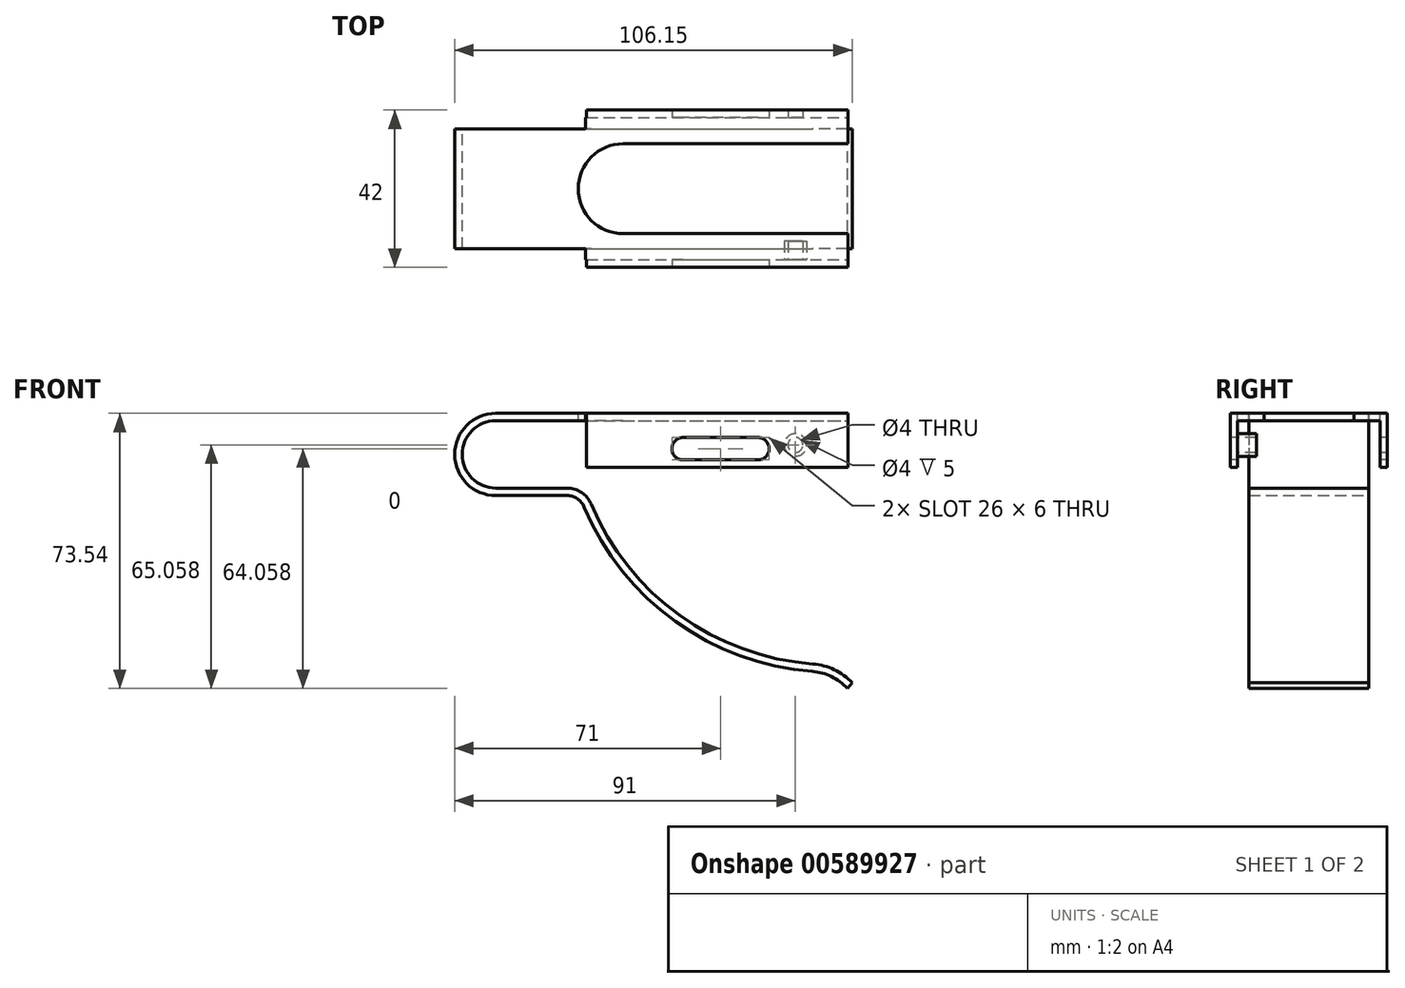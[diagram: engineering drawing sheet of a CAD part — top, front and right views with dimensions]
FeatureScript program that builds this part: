
annotation { "Feature Type Name" : "Feature", "Feature Type Description" : "" }
export const myFeature = defineFeature(function(context is Context, id is Id, definition is map)
    precondition{}
    {
        {
            var Q0;
            Q0=qCreatedBy(makeId("Front.planeOp"),FACE);
            var sketch = newSketch(context, id + "F0", { "sketchPlane" : qUnion([Q0])});
            skArc(sketch, "E0", {"start": v(0, 11) * mm, "mid": v(-11, 0) * mm, "end": v(0, -11) * mm});
            skLineSegment(sketch, "E1", {"start": v(0, 11) * mm, "end": v(94, 11) * mm});
            skLineSegment(sketch, "E2", {"start": v(0, -11) * mm, "end": v(19, -11) * mm});
            skArc(sketch, "E3", {"start": v(23.61, -14.06) * mm, "mid": v(47.9, -44.6) * mm, "end": v(84.55, -58) * mm});
            skArc(sketch, "E4", {"start": v(93.86, -62.54) * mm, "mid": v(89.64, -59.38) * mm, "end": v(84.55, -58) * mm});
            skPoint(sketch, "E5.visualSharp", {"position": v(22.4, -11) * mm});
            skArc(sketch, "E5.filletArc", {"start": v(23.61, -14.06) * mm, "mid": v(21.77, -11.84) * mm, "end": v(19, -11) * mm});
            skLineSegment(sketch, "E6.0", {"start": v(0, 9) * mm, "end": v(94, 9) * mm});
            skArc(sketch, "E6.1", {"start": v(0, 9) * mm, "mid": v(-9, 0) * mm, "end": v(0, -9) * mm});
            skArc(sketch, "E6.2", {"start": v(95.15, -61) * mm, "mid": v(90.4, -57.52) * mm, "end": v(84.7, -56) * mm});
            skArc(sketch, "E6.3", {"start": v(25.45, -13.3) * mm, "mid": v(49.07, -42.99) * mm, "end": v(84.7, -56) * mm});
            skArc(sketch, "E6.4", {"start": v(25.45, -13.3) * mm, "mid": v(22.88, -10.17) * mm, "end": v(19, -9) * mm});
            skLineSegment(sketch, "E6.5", {"start": v(0, -9) * mm, "end": v(19, -9) * mm});
            skLineSegment(sketch, "E7", {"start": v(94, 9) * mm, "end": v(94, 11) * mm});
            skLineSegment(sketch, "E8", {"start": v(93.86, -62.54) * mm, "end": v(95.15, -61) * mm});
            skLineSegment(sketch, "E9", {"start": v(97.48, -61.06) * mm, "end": v(102.9, -61.06) * mm, "construction": true});
            skPoint(sketch, "E10.newPointA", {"position": v(19, -11) * mm});
            skSolve(sketch);
        }
        {
            var Q0;
            Q0 = qSketchRegion(id + "F0", true);
            extrude(context, id + "F1", {"entities" : qUnion([Q0]), "depth" : 16 * mm, "offsetDistance" : 25 * mm});
        }
        {
            var Q0;
            Q0=makeQuery(id+"F1.opExtrude","SWEPT_FACE",FACE,{"disambiguationData":[OSD([sQuery(id+"F0.wireOp",EDGE,"E1")])]});
            var sketch = newSketch(context, id + "F2", { "sketchPlane" : qUnion([Q0])});
            skSolve(sketch);
        }
        {
            var Q0;
            {var subQ0=sQuery(id+"F0.wireOp",EDGE,"E1");Q0=makeQuery(id+"F2.imprint","IMPRINT",FACE,{"disambiguationData":[TD([[makeQuery(id+"F2.imprint","IMPRINT",EDGE,{"derivedFrom":makeQuery(id+"F1.opExtrude","CAP_EDGE",EDGE,{"disambiguationData":[OSD([subQ0])],"isStart":true})}),-1.0]])]});}
            var sketch = newSketch(context, id + "F3", { "sketchPlane" : qUnion([Q0])});
            skLineSegment(sketch, "E11.bottom", {"start": v(24, -19) * mm, "end": v(94, -19) * mm});
            skLineSegment(sketch, "E11.top", {"start": v(24, -16) * mm, "end": v(94, -16) * mm});
            skLineSegment(sketch, "E11.left", {"start": v(24, -19) * mm, "end": v(24, -16) * mm});
            skLineSegment(sketch, "E11.right", {"start": v(94, -19) * mm, "end": v(94, -16) * mm});
            skSolve(sketch);
        }
        {
            var Q0;
            Q0 = qSketchRegion(id + "F3", true);
            extrude(context, id + "F4", {"entities" : qUnion([Q0]), "operationType" : NewBodyOperationType.ADD, "oppositeDirection" : true, "depth" : 2 * mm, "offsetDistance" : 25 * mm});
        }
        {
            var Q0;
            Q0=makeQuery(id+"F4.opExtrude","SWEPT_FACE",FACE,{"disambiguationData":[OSD([sQuery(id+"F3.wireOp",EDGE,"E11.bottom")])]});
            var sketch = newSketch(context, id + "F5", { "sketchPlane" : qUnion([Q0])});
            skLineSegment(sketch, "E12.bottom", {"start": v(24.19, 11) * mm, "end": v(94, 11) * mm});
            skLineSegment(sketch, "E12.top", {"start": v(24.19, -3.48) * mm, "end": v(94, -3.48) * mm});
            skLineSegment(sketch, "E12.left", {"start": v(24.19, 11) * mm, "end": v(24.19, -3.48) * mm});
            skLineSegment(sketch, "E12.right", {"start": v(94, 11) * mm, "end": v(94, -3.48) * mm});
            skSolve(sketch);
        }
        {
            var Q0;
            Q0 = qSketchRegion(id + "F5", true);
            extrude(context, id + "F6", {"entities" : qUnion([Q0]), "operationType" : NewBodyOperationType.ADD, "depth" : 2 * mm, "offsetDistance" : 25 * mm});
        }
        {
            var Q0;
            Q0=makeQuery(id+"F1.opExtrude","SWEPT_BODY",BODY,{"disambiguationData":[OSD([sQuery(id+"F0.wireOp",EDGE,"E0"),sQuery(id+"F0.wireOp",EDGE,"E1"),sQuery(id+"F0.wireOp",EDGE,"E2"),sQuery(id+"F0.wireOp",EDGE,"E3"),sQuery(id+"F0.wireOp",EDGE,"E4"),sQuery(id+"F0.wireOp",EDGE,"E6.0"),sQuery(id+"F0.wireOp",EDGE,"E6.1"),sQuery(id+"F0.wireOp",EDGE,"E6.2"),sQuery(id+"F0.wireOp",EDGE,"E6.3"),sQuery(id+"F0.wireOp",EDGE,"E6.4"),sQuery(id+"F0.wireOp",EDGE,"E6.5"),sQuery(id+"F0.wireOp",EDGE,"E7"),sQuery(id+"F0.wireOp",EDGE,"E8"),sQuery(id+"F0.wireOp",EDGE,"E5.filletArc")])]});
            var Q1;
            Q1=makeQuery(id+"F0.imprint","IMPRINT",FACE,{"disambiguationData":[TD([[makeQuery(id+"F0.imprint","IMPRINT",EDGE,{"derivedFrom":sQuery(id+"F0.wireOp",EDGE,"E0")}),1.0]])]});
            mirror(context, id + "F7", {"operationType" : NewBodyOperationType.ADD, "entities" : qUnion([Q0]), "mirrorPlane" : qUnion([Q1])});
        }
        {
            var Q0;
            {var subQ0=makeQuery(id+"F6.boolean.opBoolean","MERGE",FACE,{"derivedFrom":[makeQuery(id+"F4.boolean.opBoolean","MERGE",FACE,{"derivedFrom":[makeQuery(id+"F1.opExtrude","SWEPT_FACE",FACE,{"disambiguationData":[OSD([sQuery(id+"F0.wireOp",EDGE,"E1")])]}),makeQuery(id+"F4.opExtrude","CAP_FACE",FACE,{"disambiguationData":[OSD([sQuery(id+"F3.wireOp",EDGE,"E11.bottom"),sQuery(id+"F3.wireOp",EDGE,"E11.top"),sQuery(id+"F3.wireOp",EDGE,"E11.left"),sQuery(id+"F3.wireOp",EDGE,"E11.right")])],"isStart":true})]}),makeQuery(id+"F6.opExtrude","SWEPT_FACE",FACE,{"disambiguationData":[OSD([sQuery(id+"F5.wireOp",EDGE,"E12.bottom")])]})]});Q0=makeQuery(id+"F7.boolean.opBoolean","MERGE",FACE,{"derivedFrom":[subQ0,makeQuery(id+"F7.opPattern","COPY",FACE,{"derivedFrom":subQ0,"instanceName":"1"})]});}
            var sketch = newSketch(context, id + "F8", { "sketchPlane" : qUnion([Q0])});
            skArc(sketch, "E13", {"start": v(34, 12) * mm, "mid": v(22, 0) * mm, "end": v(34, -12) * mm});
            skLineSegment(sketch, "E14", {"start": v(34, -12) * mm, "end": v(94, -12) * mm});
            skLineSegment(sketch, "E15", {"start": v(34, 12) * mm, "end": v(94, 12) * mm});
            skLineSegment(sketch, "E16", {"start": v(94, -12) * mm, "end": v(94, 12) * mm});
            skSolve(sketch);
        }
        {
            var Q0;
            Q0=makeQuery(id+"F8.imprint","IMPRINT",FACE,{"disambiguationData":[TD([[makeQuery(id+"F8.imprint","IMPRINT",EDGE,{"derivedFrom":sQuery(id+"F8.wireOp",EDGE,"E13")}),1.0]])]});
            extrude(context, id + "F9", {"entities" : qUnion([Q0]), "operationType" : NewBodyOperationType.REMOVE, "oppositeDirection" : true, "depth" : 2 * mm, "offsetDistance" : 25 * mm});
        }
        {
            var Q0;
            Q0=makeQuery(id+"F6.opExtrude","CAP_FACE",FACE,{"disambiguationData":[OSD([sQuery(id+"F5.wireOp",EDGE,"E12.bottom"),sQuery(id+"F5.wireOp",EDGE,"E12.top"),sQuery(id+"F5.wireOp",EDGE,"E12.left"),sQuery(id+"F5.wireOp",EDGE,"E12.right")])],"isStart":false});
            var sketch = newSketch(context, id + "F10", { "sketchPlane" : qUnion([Q0])});
            skLineSegment(sketch, "E17", {"start": v(23.7, 0) * mm, "end": v(-14.91, 0) * mm});
            skLineSegment(sketch, "E18", {"start": v(0, 23.08) * mm, "end": v(0, -22.73) * mm});
            skLineSegment(sketch, "E19", {"start": v(50, 1.52) * mm, "end": v(70, 1.52) * mm});
            skArc(sketch, "E20.0.startCap", {"start": v(50, -1.48) * mm, "mid": v(47, 1.52) * mm, "end": v(50, 4.52) * mm});
            skArc(sketch, "E20.0.endCap", {"start": v(70, 4.52) * mm, "mid": v(73, 1.52) * mm, "end": v(70, -1.48) * mm});
            skLineSegment(sketch, "E20.0.left", {"start": v(50, 4.52) * mm, "end": v(70, 4.52) * mm});
            skLineSegment(sketch, "E20.0.right", {"start": v(50, -1.48) * mm, "end": v(70, -1.48) * mm});
            skSolve(sketch);
        }
        {
            var Q0;
            Q0 = qSketchRegion(id + "F10", true);
            extrude(context, id + "F11", {"entities" : qUnion([Q0]), "operationType" : NewBodyOperationType.REMOVE, "endBound" : BoundingType.THROUGH_ALL, "oppositeDirection" : true, "depth" : 25 * mm, "offsetDistance" : 25 * mm});
        }
        {
            var Q0;
            Q0=qCreatedBy(makeId("Front.planeOp"),FACE);
            var sketch = newSketch(context, id + "F12", { "sketchPlane" : qUnion([Q0])});
            skPoint(sketch, "E21", {"position": v(80, 2.52) * mm});
            skSolve(sketch);
        }
        {
            var Q0;
            Q0=sQuery(id+"F12.wireOp",VERTEX,"E21");
            var Q1;
            Q1=makeQuery(id+"F1.opExtrude","SWEPT_BODY",BODY,{"disambiguationData":[OSD([sQuery(id+"F0.wireOp",EDGE,"E0"),sQuery(id+"F0.wireOp",EDGE,"E1"),sQuery(id+"F0.wireOp",EDGE,"E2"),sQuery(id+"F0.wireOp",EDGE,"E3"),sQuery(id+"F0.wireOp",EDGE,"E4"),sQuery(id+"F0.wireOp",EDGE,"E6.0"),sQuery(id+"F0.wireOp",EDGE,"E6.1"),sQuery(id+"F0.wireOp",EDGE,"E6.2"),sQuery(id+"F0.wireOp",EDGE,"E6.3"),sQuery(id+"F0.wireOp",EDGE,"E6.4"),sQuery(id+"F0.wireOp",EDGE,"E6.5"),sQuery(id+"F0.wireOp",EDGE,"E7"),sQuery(id+"F0.wireOp",EDGE,"E8"),sQuery(id+"F0.wireOp",EDGE,"E5.filletArc")])]});
            hole(context, id + "F13", {"style" : HoleStyle.SIMPLE, "endStyle" : HoleEndStyle.THROUGH, "holeDiameter" : 4 * mm, "majorDiameter" : 5 * mm, "isTappedThrough" : true, "tappedDepth" : 12 * mm, "tapClearance" : 3, "locations" : qUnion([Q0]), "scope" : qUnion([Q1])});
        }
        {
            var Q0;
            Q0=makeQuery(id+"F6.opExtrude","CAP_FACE",FACE,{"disambiguationData":[OSD([sQuery(id+"F5.wireOp",EDGE,"E12.bottom"),sQuery(id+"F5.wireOp",EDGE,"E12.top"),sQuery(id+"F5.wireOp",EDGE,"E12.left"),sQuery(id+"F5.wireOp",EDGE,"E12.right")])],"isStart":true});
            var sketch = newSketch(context, id + "F14", { "sketchPlane" : qUnion([Q0])});
            skCircle(sketch, "E22.0", {"center": v(-80, 2.52) * mm, "radius": 2 * mm});
            skCircle(sketch, "E23.0", {"center": v(-80, 2.52) * mm, "radius": 3 * mm});
            skSolve(sketch);
        }
        {
            var Q0;
            Q0 = qSketchRegion(id + "F14", true);
            extrude(context, id + "F15", {"entities" : qUnion([Q0]), "operationType" : NewBodyOperationType.ADD, "depth" : 5 * mm, "offsetDistance" : 25 * mm});
        }
    });
